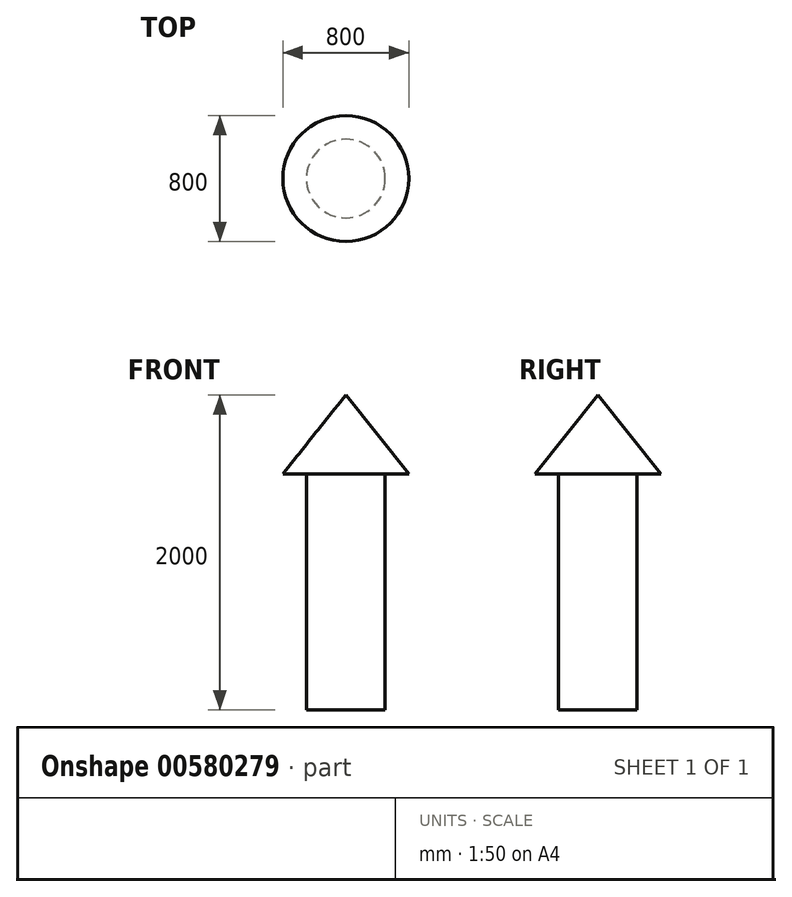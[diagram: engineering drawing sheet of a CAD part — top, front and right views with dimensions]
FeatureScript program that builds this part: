
annotation { "Feature Type Name" : "Feature", "Feature Type Description" : "" }
export const myFeature = defineFeature(function(context is Context, id is Id, definition is map)
    precondition{}
    {
        {
            var Q0;
            Q0=qCreatedBy(makeId("Top.planeOp"),FACE);
            var sketch = newSketch(context, id + "F0", { "sketchPlane" : qUnion([Q0])});
            skCircle(sketch, "E0", {"center": v(0, 0) * mm, "radius": 250 * mm});
            skSolve(sketch);
        }
        {
            var Q0;
            Q0=makeQuery(id+"F0.imprint","IMPRINT",FACE,{"disambiguationData":[TD([[makeQuery(id+"F0.imprint","IMPRINT",EDGE,{"derivedFrom":sQuery(id+"F0.wireOp",EDGE,"E0")}),1.0]])]});
            extrude(context, id + "F1", {"entities" : qUnion([Q0]), "depth" : 1500 * mm, "offsetDistance" : 25 * mm});
        }
        {
            var Q0;
            Q0=qCreatedBy(makeId("Front.planeOp"),FACE);
            var sketch = newSketch(context, id + "F2", { "sketchPlane" : qUnion([Q0])});
            skLineSegment(sketch, "E1", {"start": v(0, 1500) * mm, "end": v(400, 1500) * mm});
            skLineSegment(sketch, "E2", {"start": v(0, 1500) * mm, "end": v(0, 2000) * mm});
            skLineSegment(sketch, "E3", {"start": v(0, 2000) * mm, "end": v(400, 1500) * mm});
            skSolve(sketch);
        }
        {
            var Q0;
            Q0 = qSketchRegion(id + "F2", true);
            var Q1;
            Q1=sQuery(id+"F2.wireOp",EDGE,"E2");
            revolve(context, id + "F3", {"operationType" : NewBodyOperationType.ADD, "entities" : qUnion([Q0]), "axis" : qUnion([Q1]), "revolveType" : RevolveType.FULL});
        }
    });
